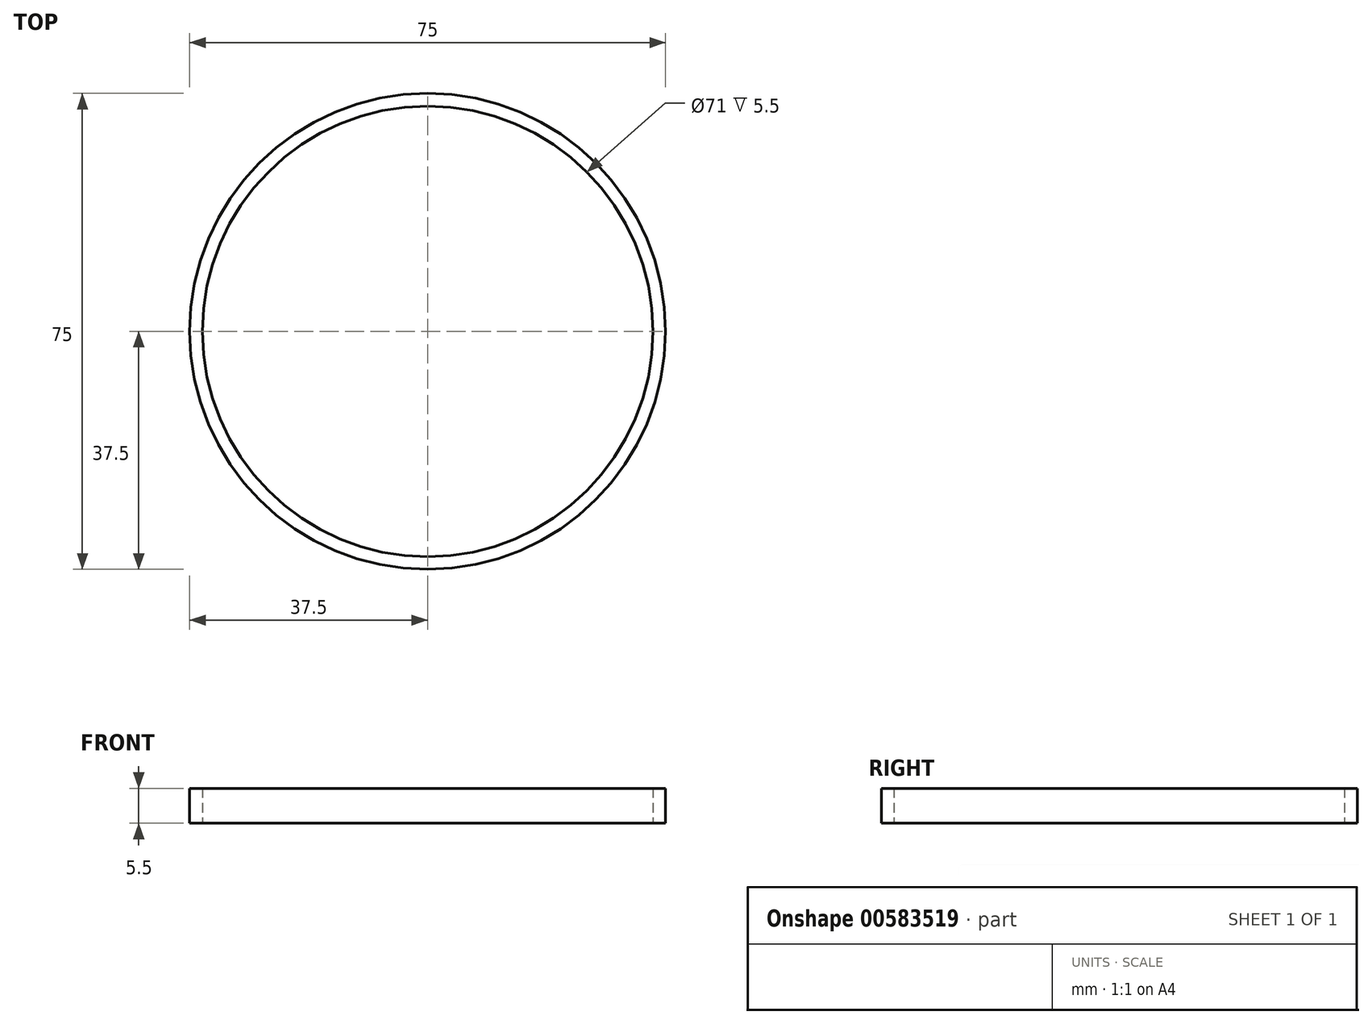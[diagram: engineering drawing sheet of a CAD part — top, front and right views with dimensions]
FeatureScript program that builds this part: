
annotation { "Feature Type Name" : "Feature", "Feature Type Description" : "" }
export const myFeature = defineFeature(function(context is Context, id is Id, definition is map)
    precondition{}
    {
        {
            var Q0;
            Q0=qCreatedBy(makeId("Top.planeOp"),FACE);
            var sketch = newSketch(context, id + "F0", { "sketchPlane" : qUnion([Q0])});
            skCircle(sketch, "E0", {"center": v(0, 0) * mm, "radius": 35.5 * mm});
            skCircle(sketch, "E1", {"center": v(0, 0) * mm, "radius": 37.5 * mm});
            skSolve(sketch);
        }
        {
            var Q0;
            Q0 = qSketchRegion(id + "F0", true);
            extrude(context, id + "F1", {"entities" : qUnion([Q0]), "depth" : 5.5 * mm, "offsetDistance" : 25 * mm});
        }
    });
